# Revit family: Kal_A3-Aluminium-Sliding-Single-sidelight
name_source: partatom
category: Doors
revit_build: Autodesk Revit 2016 (Build: 20150220_1215(x64)
units: mm (PartAtom-declared; Revit-internal decimal feet)

## family parameters
Always vertical = Yes
Cut with Voids When Loaded = No
Host = Wall
Room Calculation Point = No
Shared = No

## types (8) — shared parameters
Construction Type = ALUMINIUM
Frame Finish = ALUMINIUM
Function = Interior
Height = 2125 mm  [stored 6.97178 ft]
Material Door Frame = Default ALUMINIUM FRAME
Material Glass = Glass
Model Type = Single Sliding
Wall Closure = By host
zero-valued in all types: Rough Height, Rough Width, Thickness

## per-type parameters (varying)
| type | Width | dw | ww |
| 600SL - 1500DOOR RH | 2100 mm | 1500 mm | 600 mm |
| 600SL -1800DOOR RH | 2400 mm  [stored 7.87402 ft] | 1800 mm | 600 mm |
| 600SL - 2100DOOR RH | 2700 mm  [stored 8.85827 ft] | 2100 mm | 600 mm |
| 600SL - 2400DOOR RH | 3000 mm  [stored 9.84252 ft] | 2400 mm  [stored 7.87402 ft] | 600 mm |
| 900SL 1500DOOR RH | 2400 mm  [stored 7.87402 ft] | 1500 mm | 900 mm |
| 900SL 1800DOOR RH | 2700 mm  [stored 8.85827 ft] | 1800 mm | 900 mm |
| 900SL 2100DOOR RH | 3000 mm  [stored 9.84252 ft] | 2100 mm | 900 mm |
| 900SL 2400DOOR RH | 3300 mm | 2400 mm  [stored 7.87402 ft] | 900 mm |

note: [stored X ft] marks values corroborated as IEEE doubles in the binary element streams (Revit-internal decimal feet)

## geometry (parser evidence)
native form markers: Sweep x7
no freeform markers — native parametric forms only
